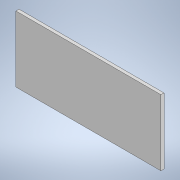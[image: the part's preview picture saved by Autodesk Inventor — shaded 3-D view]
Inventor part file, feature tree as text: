
AUTODESK INVENTOR PART (.ipt)
format: ipt  version: 2021 (Build 250183000, 183)  size: 89,088 bytes
history: native  units: mm
features: extrude x1, sketch x1
ambient origin geometry x8: Origin, YZ Plane, XZ Plane, XY Plane, X Axis, Y Axis, Z Axis, Center Point
bodies: Solid1 (feature_tree)
feature tree (2):
  extrude  "Extrusion1"  Depth=42.5mm
  sketch  "Sketch1"  dims[d0=93.5mm d1=42.5mm d2=2.0mm d3=0.0mm]
